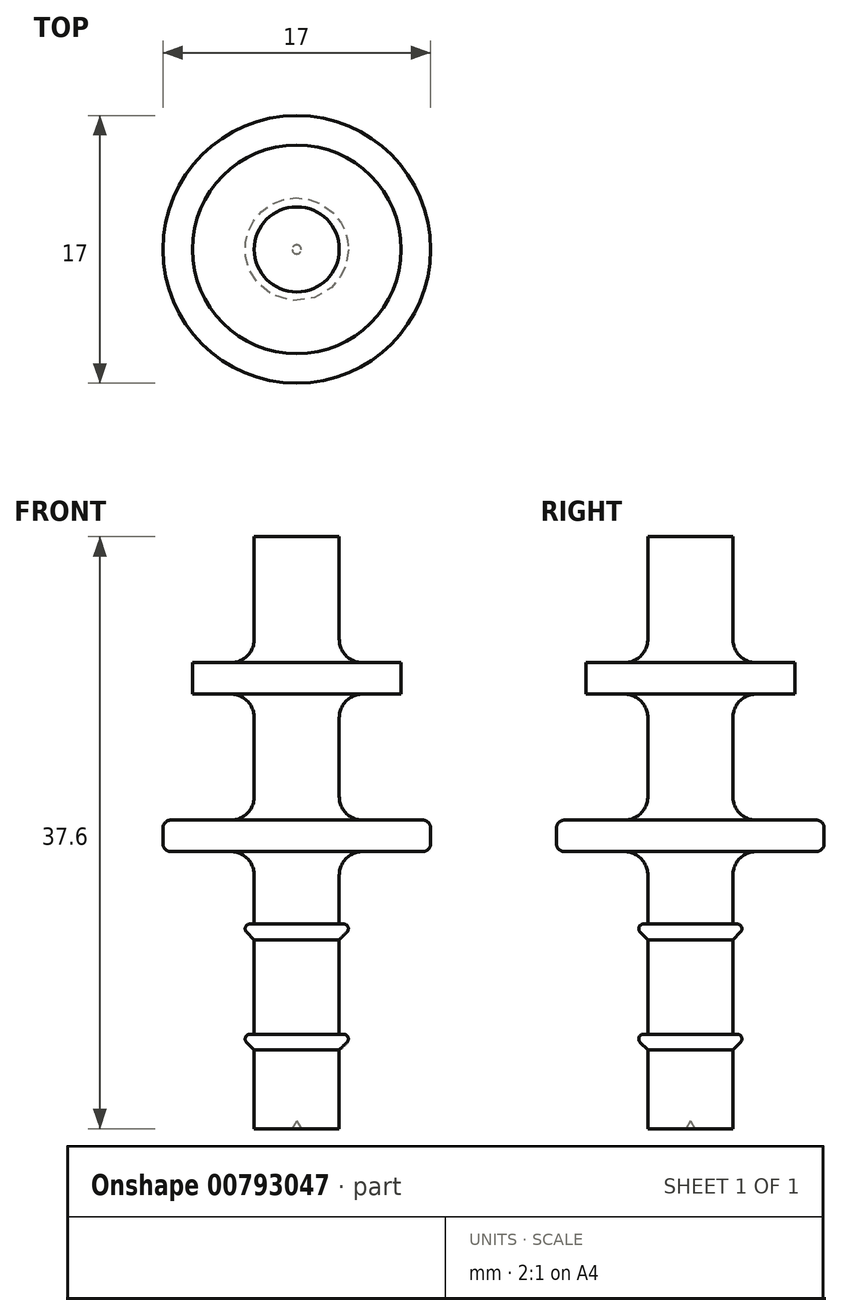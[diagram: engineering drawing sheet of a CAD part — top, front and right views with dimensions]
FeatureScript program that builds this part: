
annotation { "Feature Type Name" : "Feature", "Feature Type Description" : "" }
export const myFeature = defineFeature(function(context is Context, id is Id, definition is map)
    precondition{}
    {
        {
            var Q0;
            Q0=qCreatedBy(makeId("Front.planeOp"),FACE);
            var sketch = newSketch(context, id + "F0", { "sketchPlane" : qUnion([Q0])});
            skLineSegment(sketch, "E0", {"start": v(-27.58, -23.45) * mm, "end": v(-27.58, -18.45) * mm});
            skLineSegment(sketch, "E1", {"start": v(-27.85, -17.45) * mm, "end": v(-27.58, -17.45) * mm});
            skLineSegment(sketch, "E2", {"start": v(-27.58, -17.45) * mm, "end": v(-27.58, -11.45) * mm});
            skLineSegment(sketch, "E3", {"start": v(-27.85, -10.45) * mm, "end": v(-27.58, -10.45) * mm});
            skLineSegment(sketch, "E4", {"start": v(-27.58, -10.45) * mm, "end": v(-27.58, -7.35) * mm});
            skLineSegment(sketch, "E5", {"start": v(-29.08, -5.85) * mm, "end": v(-32.88, -5.85) * mm});
            skLineSegment(sketch, "E6", {"start": v(-33.38, -5.35) * mm, "end": v(-33.38, -4.35) * mm});
            skLineSegment(sketch, "E7", {"start": v(-32.88, -3.85) * mm, "end": v(-29.08, -3.85) * mm});
            skLineSegment(sketch, "E8", {"start": v(-27.58, -2.35) * mm, "end": v(-27.58, 2.65) * mm});
            skLineSegment(sketch, "E9", {"start": v(-29.08, 4.15) * mm, "end": v(-31.5, 4.15) * mm});
            skLineSegment(sketch, "E10", {"start": v(-31.5, 4.15) * mm, "end": v(-31.5, 6.15) * mm});
            skLineSegment(sketch, "E11", {"start": v(-31.5, 6.15) * mm, "end": v(-29.08, 6.15) * mm});
            skLineSegment(sketch, "E12", {"start": v(-27.58, 7.65) * mm, "end": v(-27.58, 14.15) * mm});
            skLineSegment(sketch, "E13", {"start": v(-27.58, 14.15) * mm, "end": v(-24.88, 14.15) * mm});
            skPoint(sketch, "E14.visualSharp", {"position": v(-33.38, -3.85) * mm});
            skArc(sketch, "E14.filletArc", {"start": v(-32.88, -3.85) * mm, "mid": v(-33.23, -4) * mm, "end": v(-33.38, -4.35) * mm});
            skPoint(sketch, "E15.visualSharp", {"position": v(-33.38, -5.85) * mm});
            skArc(sketch, "E15.filletArc", {"start": v(-33.38, -5.35) * mm, "mid": v(-33.23, -5.7) * mm, "end": v(-32.88, -5.85) * mm});
            skLineSegment(sketch, "E16", {"start": v(-24.88, 14.15) * mm, "end": v(-24.88, -22.95) * mm});
            skLineSegment(sketch, "E17", {"start": v(-24.88, -22.95) * mm, "end": v(-25.16, -23.45) * mm});
            skLineSegment(sketch, "E18", {"start": v(-25.16, -23.45) * mm, "end": v(-27.58, -23.45) * mm});
            skLineSegment(sketch, "E19", {"start": v(-27.58, -18.45) * mm, "end": v(-28.06, -17.96) * mm});
            skLineSegment(sketch, "E20", {"start": v(-27.58, -11.45) * mm, "end": v(-28.06, -10.96) * mm});
            skPoint(sketch, "E21.visualSharp", {"position": v(-27.58, 4.15) * mm});
            skArc(sketch, "E21.filletArc", {"start": v(-27.58, 2.65) * mm, "mid": v(-28.02, 3.71) * mm, "end": v(-29.08, 4.15) * mm});
            skPoint(sketch, "E22.visualSharp", {"position": v(-27.58, 6.15) * mm});
            skArc(sketch, "E22.filletArc", {"start": v(-29.08, 6.15) * mm, "mid": v(-28.02, 6.6) * mm, "end": v(-27.58, 7.65) * mm});
            skPoint(sketch, "E23.visualSharp", {"position": v(-27.58, -5.85) * mm});
            skArc(sketch, "E23.filletArc", {"start": v(-27.58, -7.35) * mm, "mid": v(-28.02, -6.29) * mm, "end": v(-29.08, -5.85) * mm});
            skPoint(sketch, "E24.visualSharp", {"position": v(-27.58, -3.85) * mm});
            skArc(sketch, "E24.filletArc", {"start": v(-29.08, -3.85) * mm, "mid": v(-28.02, -3.4) * mm, "end": v(-27.58, -2.35) * mm});
            skPoint(sketch, "E25.visualSharp", {"position": v(-28.58, -10.45) * mm});
            skArc(sketch, "E25.filletArc", {"start": v(-27.85, -10.45) * mm, "mid": v(-28.13, -10.63) * mm, "end": v(-28.06, -10.96) * mm});
            skPoint(sketch, "E26.visualSharp", {"position": v(-28.58, -17.45) * mm});
            skArc(sketch, "E26.filletArc", {"start": v(-27.85, -17.45) * mm, "mid": v(-28.13, -17.63) * mm, "end": v(-28.06, -17.96) * mm});
            skSolve(sketch);
        }
        {
            var Q0;
            Q0=makeQuery(id+"F0.imprint","IMPRINT",FACE,{"disambiguationData":[TD([[makeQuery(id+"F0.imprint","IMPRINT",EDGE,{"derivedFrom":sQuery(id+"F0.wireOp",EDGE,"E0")}),-1.0]])]});
            var Q1;
            Q1=sQuery(id+"F0.wireOp",EDGE,"E16");
            revolve(context, id + "F1", {"surfaceOperationType" : NewSurfaceOperationType.NEW, "entities" : qUnion([Q0]), "axis" : qUnion([Q1]), "revolveType" : RevolveType.FULL});
        }
    });
